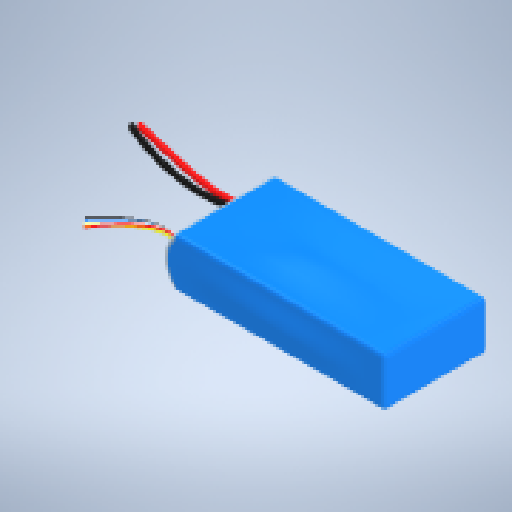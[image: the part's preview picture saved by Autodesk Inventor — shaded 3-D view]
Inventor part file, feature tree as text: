
AUTODESK INVENTOR PART (.ipt)
format: ipt  version: 2024.3 (Build 283343000, 343)  size: 536,576 bytes
history: native  units: in
note: dims shown in document units (in); Inventor stores cm internally (conversion verified against a paired STEP export)
features: other x3, direct_edit x1, sweep x1
ambient origin geometry x8: Origin, YZ Plane, XZ Plane, XY Plane, X Axis, Y Axis, Z Axis, Center Point
bodies: Solid1 (feature_tree)
feature tree (5):
  other  "Plane1"
  other  "Plane2"
  direct_edit  "Direct Edit1"
  sweep  "Sweep7"
  other  "Scale1"
